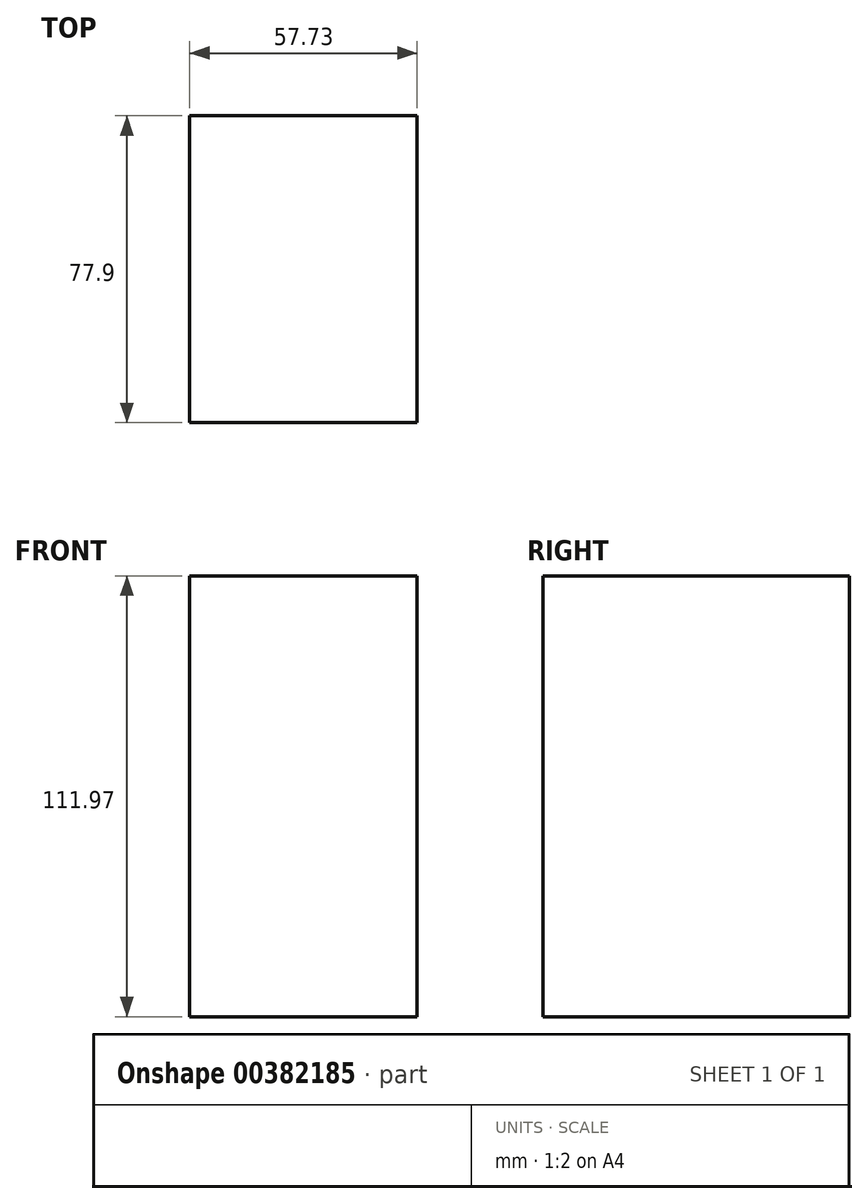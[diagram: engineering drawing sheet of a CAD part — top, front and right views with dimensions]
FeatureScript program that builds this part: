
annotation { "Feature Type Name" : "Feature", "Feature Type Description" : "" }
export const myFeature = defineFeature(function(context is Context, id is Id, definition is map)
    precondition{}
    {
        {
            var Q0;
            Q0=qCreatedBy(makeId("Top.planeOp"),FACE);
            var sketch = newSketch(context, id + "F0", { "sketchPlane" : qUnion([Q0])});
            skLineSegment(sketch, "E0.bottom", {"start": v(-26.6, 46.21) * mm, "end": v(31.13, 46.21) * mm});
            skLineSegment(sketch, "E0.top", {"start": v(-26.6, -31.7) * mm, "end": v(31.13, -31.7) * mm});
            skLineSegment(sketch, "E0.left", {"start": v(-26.6, 46.21) * mm, "end": v(-26.6, -31.7) * mm});
            skLineSegment(sketch, "E0.right", {"start": v(31.13, 46.21) * mm, "end": v(31.13, -31.7) * mm});
            skSolve(sketch);
        }
        {
            var Q0;
            Q0=makeQuery(id+"F0.imprint","IMPRINT",FACE,{"disambiguationData":[TD([[makeQuery(id+"F0.imprint","IMPRINT",EDGE,{"derivedFrom":sQuery(id+"F0.wireOp",EDGE,"E0.bottom")}),-1.0]])]});
            extrude(context, id + "F1", {"entities" : qUnion([Q0]), "depth" : 111.97 * mm});
        }
    });
